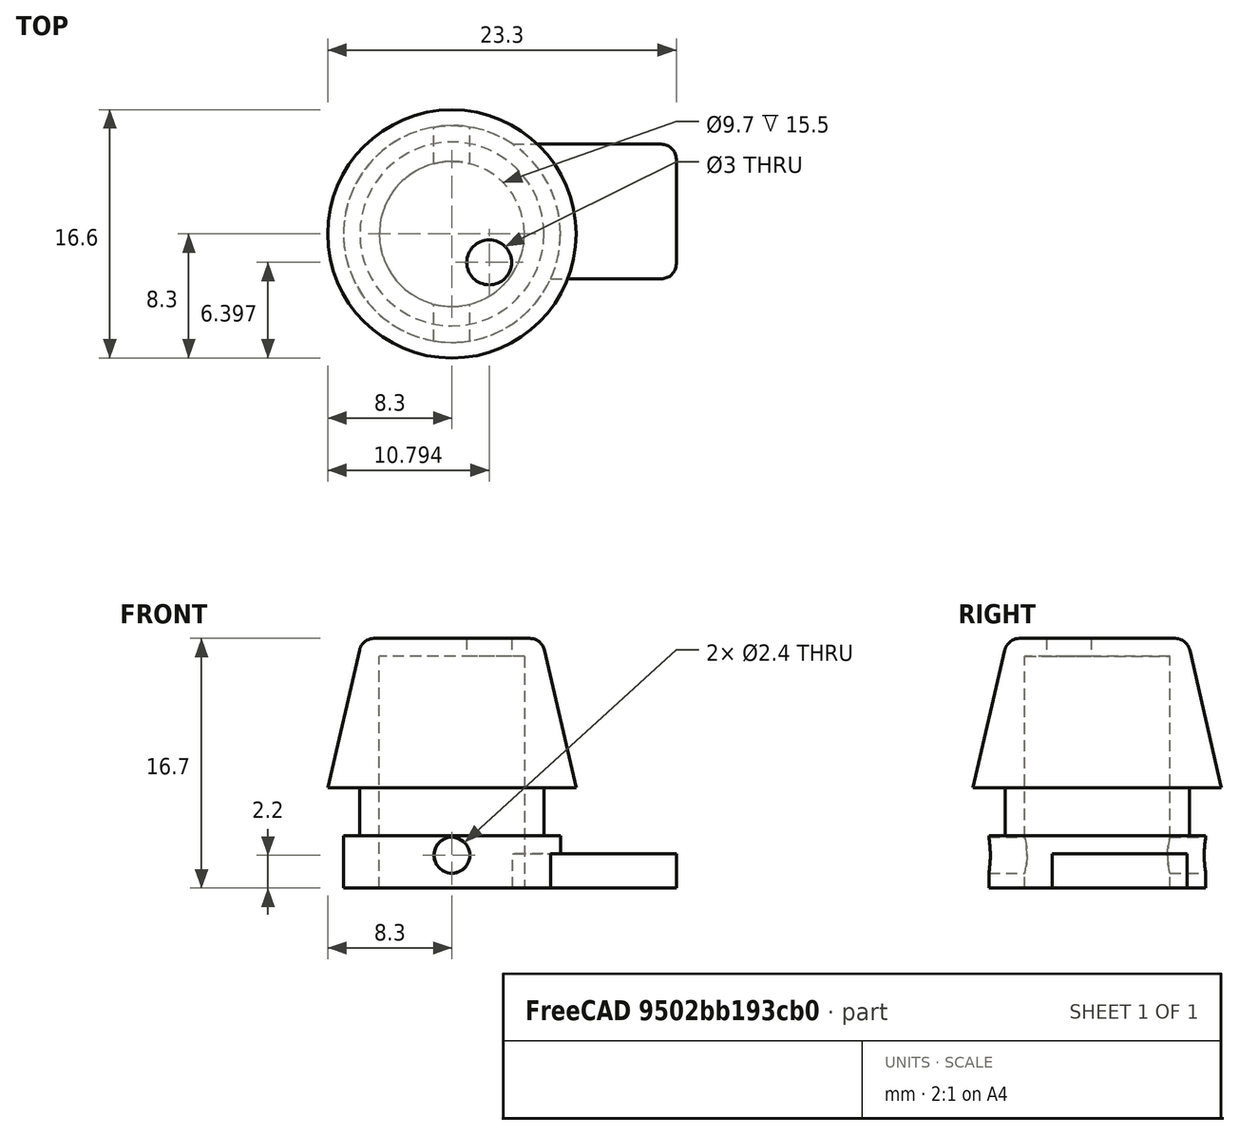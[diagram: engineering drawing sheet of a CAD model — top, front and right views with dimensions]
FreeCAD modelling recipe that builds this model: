
FCSTD DOCUMENT  (FreeCAD 0.19R19242 (Git))
Label: radio
License: All rights reserved
LicenseURL: http://en.wikipedia.org/wiki/All_rights_reserved
objects: Sketcher::SketchObject×3, Part::Cylinder×2, PartDesign::Hole×2, Part::Box×1, Part::Cone×1, Part::MultiFuse×1, PartDesign::FeatureBase×1, PartDesign::Pocket×1, Mesh::Feature×1, PartDesign::Body×1, PartDesign::Fillet×1
note: 17 computed .brp shape members not serialized (recipe doc carries the construction recipe); baked Part::Feature solids carry a one-line shape summary decoded from their .brp

FEATURE [Part::Cylinder] Cylinder
  Angle = 360
  AttacherType = Attacher::AttachEngine3D
  Height = 3.5
  Radius = 7.25
FEATURE [Part::Box] Box  label="Cube"
  AttacherType = Attacher::AttachEngine3D
  Height = 2.3
  Length = 15
  Placement = pos=(0,-3,0) rot=(0,0,1;0rad)
  Width = 9
FEATURE [Part::Cylinder] Cylinder001
  Angle = 360
  AttacherType = Attacher::AttachEngine3D
  Height = 6.7
  Radius = 6.15
FEATURE [Part::Cone] Cone
  Angle = 360
  AttacherType = Attacher::AttachEngine3D
  Height = 10
  Placement = pos=(0,0,6.7) rot=(0,0,1;0rad)
  Radius1 = 8.3
  Radius2 = 6
FEATURE [Part::MultiFuse] Fusion
  Shapes = -> [Cylinder,Cylinder001,Box,Cone]
FEATURE [PartDesign::FeatureBase] BaseFeature
  BaseFeature = -> Fusion
FEATURE [Sketcher::SketchObject] Sketch
  MapMode = 5
  Support = -> [XY_Plane]
  sketch-geometry (1):
    g0: Circle CenterX=0 CenterY=0 CenterZ=0 NormalX=0 NormalY=0 NormalZ=1 AngleXU=0 Radius=4.85
  constraints (2):
    c: Coincident(g0,g-1)
    c: Radius(g0) = 4.85
FEATURE [PartDesign::Pocket] Pocket
  BaseFeature = -> BaseFeature
  Length = 31
  Length2 = 100
  Midplane = true
  Profile = -> Sketch
  Type = 0
FEATURE [Sketcher::SketchObject] Sketch001
  AttachmentOffset = pos=(0,0,20) rot=(0,0,1;0rad)
  MapMode = 5
  Placement = pos=(0,0,20) rot=(0,0,1;0rad)
  Support = -> [XY_Plane]
  sketch-geometry (1):
    g0: Circle CenterX=2.49409 CenterY=-1.90321 CenterZ=0 NormalX=0 NormalY=0 NormalZ=1 AngleXU=0 Radius=1
  constraints (1):
    c: Radius(g0) = 1
FEATURE [PartDesign::Hole] Hole
  BaseFeature = -> Pocket
  Depth = 50
  DepthType = 0
  Diameter = 3
  DrillPoint = 1
  DrillPointAngle = 118
  HoleCutCountersinkAngle = 90
  HoleCutDepth = 0
  HoleCutDiameter = 0
  HoleCutType = 0
  ModelActualThread = false
  Profile = -> Sketch001
  Tapered = false
  TaperedAngle = 90
  ThreadAngle = 0
  ThreadClass = 0
  ThreadCutOffInner = 0
  ThreadCutOffOuter = 0
  ThreadDirection = 0
  ThreadFit = 0
  ThreadPitch = 0
  ThreadSize = 0
  ThreadType = 0
  Threaded = false
FEATURE [Mesh::Feature] Mesh  label="Body (Meshed)"
FEATURE [PartDesign::Body] Body
  BaseFeature = -> Fusion
  Group = -> [BaseFeature,Sketch,Pocket,Sketch001,Hole,Hole001,Fillet]
  Origin = -> Origin
  Tip = -> Fillet
FEATURE [Sketcher::SketchObject] Sketch002
  AttachmentOffset = pos=(0,0,10) rot=(0,0,1;0rad)
  MapMode = 3
  Placement = pos=(0,-10,2.2e-15) rot=(1,0,0;1.5708rad)
  Support = -> [Body]
  sketch-geometry (1):
    g0: Circle CenterX=0 CenterY=2.2 CenterZ=0 NormalX=0 NormalY=0 NormalZ=1 AngleXU=0 Radius=1
  constraints (3):
    c: PointOnObject(g0,g-2)
    c: Radius(g0) = 1
    c: DistanceY(g-1,g0) = 2.2
FEATURE [PartDesign::Hole] Hole001
  BaseFeature = -> Hole
  Depth = 225
  DepthType = 0
  Diameter = 2.4
  DrillPoint = 1
  DrillPointAngle = 118
  HoleCutCountersinkAngle = 90
  HoleCutDepth = 0
  HoleCutDiameter = 0
  HoleCutType = 0
  ModelActualThread = false
  Profile = -> Sketch002
  Tapered = false
  TaperedAngle = 90
  ThreadAngle = 0
  ThreadClass = 0
  ThreadCutOffInner = 0
  ThreadCutOffOuter = 0
  ThreadDirection = 0
  ThreadFit = 0
  ThreadPitch = 0
  ThreadSize = 0
  ThreadType = 0
  Threaded = false
FEATURE [PartDesign::Fillet] Fillet
  Base = -> Hole001 [Edge14,Edge19,Edge42]
  BaseFeature = -> Hole001
  Radius = 1
